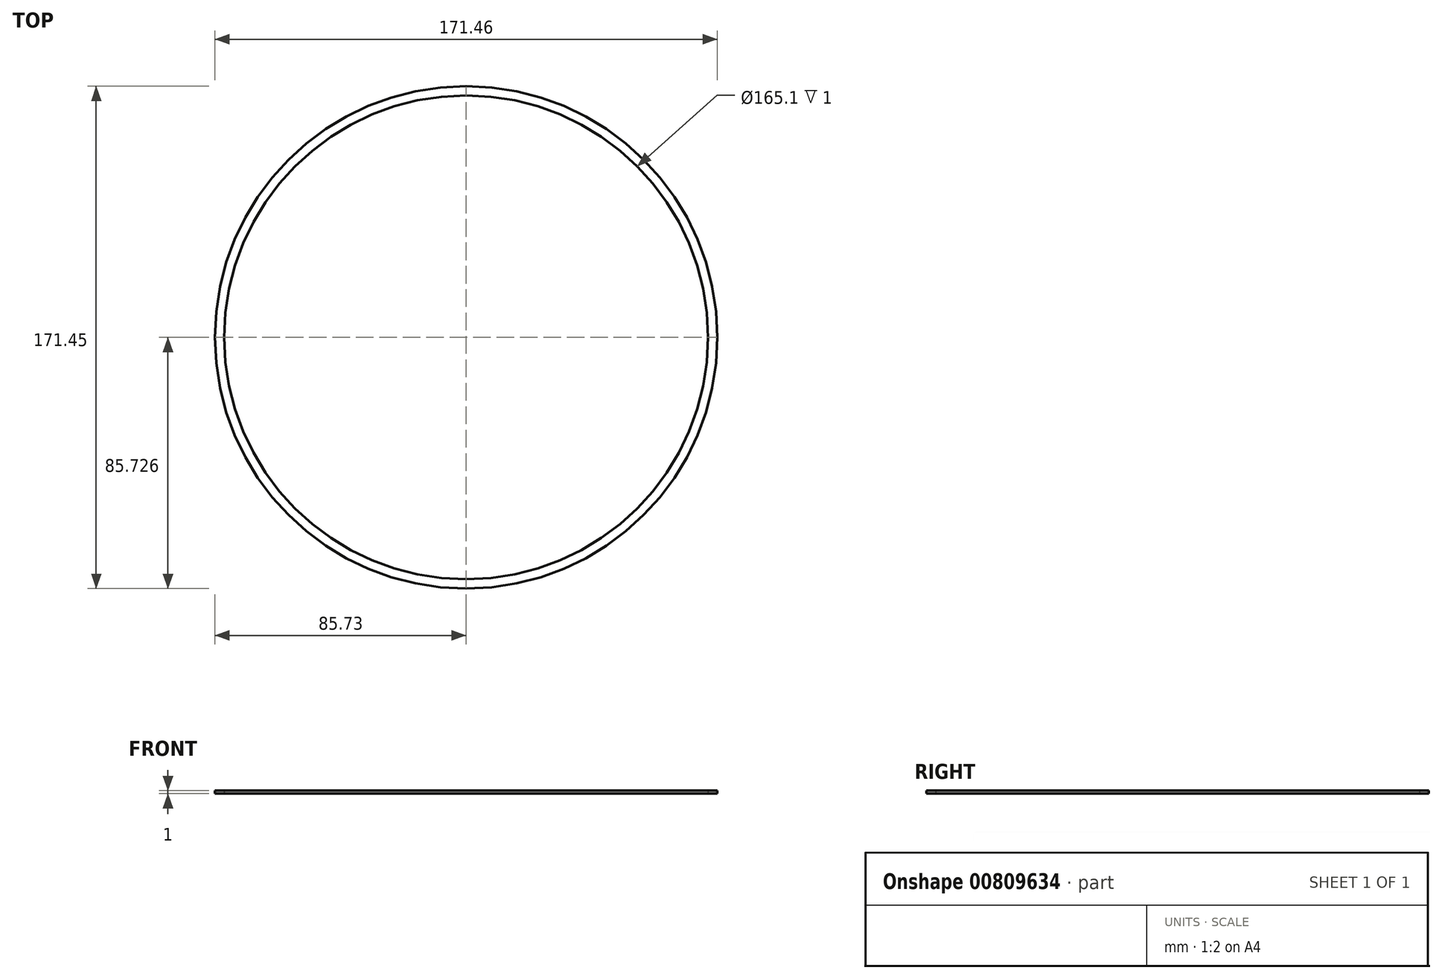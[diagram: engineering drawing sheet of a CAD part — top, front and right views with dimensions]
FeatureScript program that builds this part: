
annotation { "Feature Type Name" : "Feature", "Feature Type Description" : "" }
export const myFeature = defineFeature(function(context is Context, id is Id, definition is map)
    precondition{}
    {
        {
            var Q0;
            Q0=qCreatedBy(makeId("Top.planeOp"),FACE);
            var sketch = newSketch(context, id + "F0", { "sketchPlane" : qUnion([Q0])});
            skCircle(sketch, "E0", {"center": v(0, -3.83) * mm, "radius": 82.55 * mm});
            skCircle(sketch, "E1", {"center": v(0, -3.83) * mm, "radius": 85.73 * mm});
            skSolve(sketch);
        }
        {
            var Q0;
            Q0=makeQuery(id+"F0.imprint","IMPRINT",FACE,{"disambiguationData":[TD([[makeQuery(id+"F0.imprint","IMPRINT",EDGE,{"derivedFrom":sQuery(id+"F0.wireOp",EDGE,"E0")}),-1.0]])]});
            extrude(context, id + "F1", {"entities" : qUnion([Q0]), "depth" : 1 * mm, "offsetDistance" : 25.4 * mm});
        }
    });
